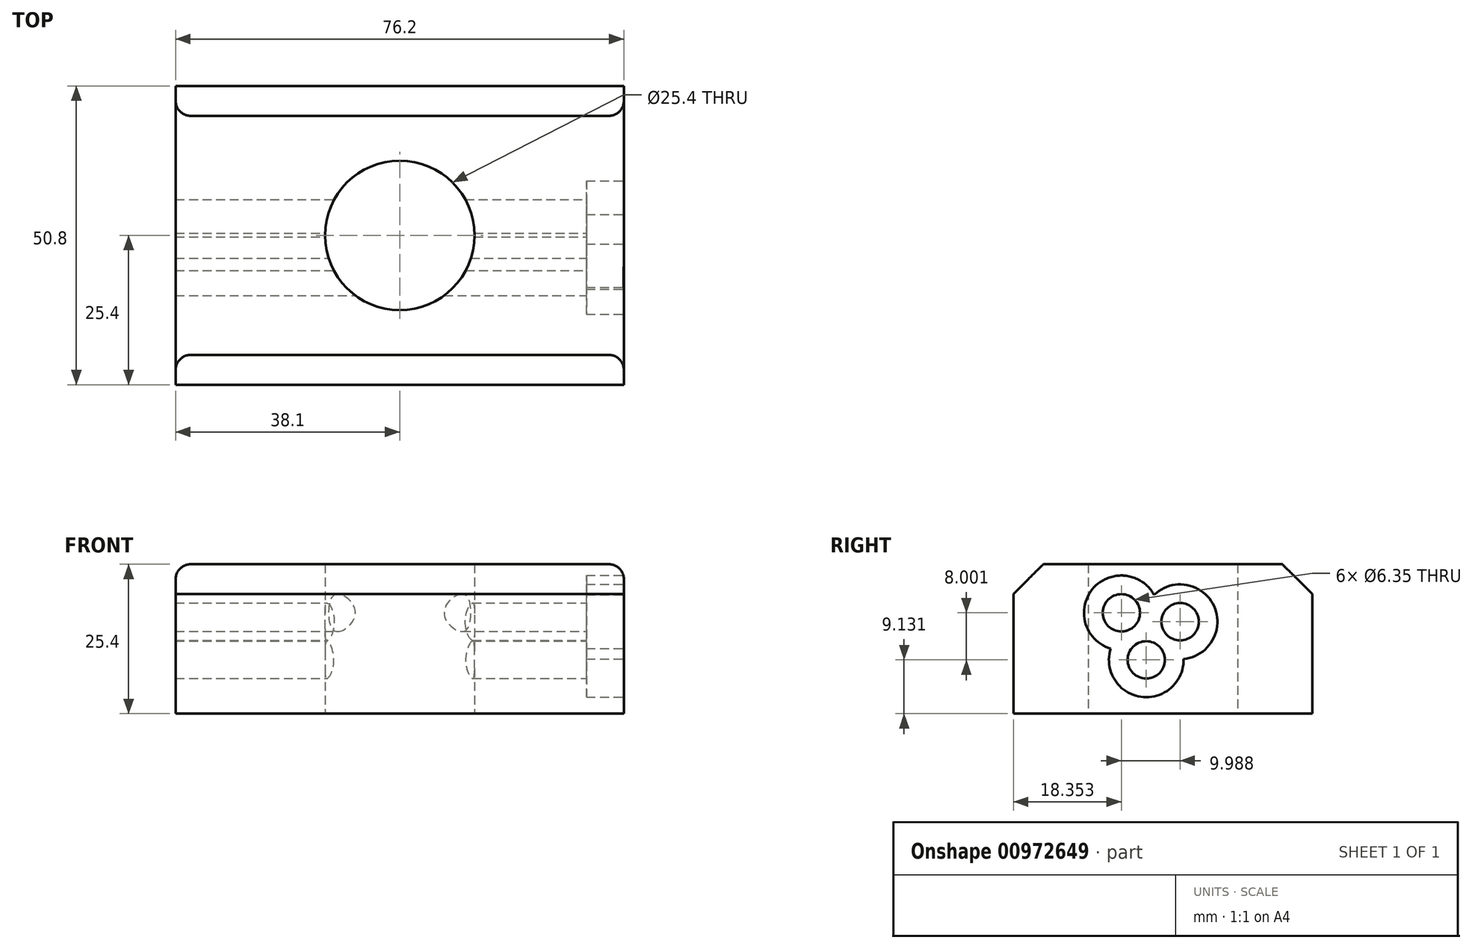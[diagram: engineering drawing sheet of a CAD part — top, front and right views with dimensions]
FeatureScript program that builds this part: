
annotation { "Feature Type Name" : "Feature", "Feature Type Description" : "" }
export const myFeature = defineFeature(function(context is Context, id is Id, definition is map)
    precondition{}
    {
        {
            var Q0;
            Q0=qCreatedBy(makeId("Top.planeOp"),FACE);
            var sketch = newSketch(context, id + "F0", { "sketchPlane" : qUnion([Q0])});
            skLineSegment(sketch, "E0.bottom", {"start": v(-38.1, 25.4) * mm, "end": v(38.1, 25.4) * mm});
            skLineSegment(sketch, "E0.top", {"start": v(-38.1, -25.4) * mm, "end": v(38.1, -25.4) * mm});
            skLineSegment(sketch, "E0.left", {"start": v(-38.1, 25.4) * mm, "end": v(-38.1, -25.4) * mm});
            skLineSegment(sketch, "E0.right", {"start": v(38.1, 25.4) * mm, "end": v(38.1, -25.4) * mm});
            skPoint(sketch, "E0.middle", {"position": v(0, 0) * mm});
            skCircle(sketch, "E1", {"center": v(0, 0) * mm, "radius": 12.7 * mm});
            skSolve(sketch);
        }
        {
            var Q0;
            Q0=makeQuery(id+"F0.imprint","IMPRINT",FACE,{"disambiguationData":[TD([[makeQuery(id+"F0.imprint","IMPRINT",EDGE,{"derivedFrom":sQuery(id+"F0.wireOp",EDGE,"E0.bottom")}),-1.0]])]});
            extrude(context, id + "F1", {"entities" : qUnion([Q0]), "depth" : 25.4 * mm, "offsetDistance" : 25.4 * mm});
        }
        {
            var Q0;
            Q0=makeQuery(id+"F1.opExtrude","SWEPT_FACE",FACE,{"disambiguationData":[OSD([sQuery(id+"F0.wireOp",EDGE,"E0.right")])]});
            var sketch = newSketch(context, id + "F2", { "sketchPlane" : qUnion([Q0])});
            skCircle(sketch, "E2", {"center": v(-2.34, 14.5) * mm, "radius": 5.4 * mm});
            skPoint(sketch, "E2.first.point", {"position": v(-7.05, 17.13) * mm});
            skPoint(sketch, "E2.second.point", {"position": v(2.94, 15.62) * mm});
            skPoint(sketch, "E2.third.point", {"position": v(-2.81, 9.13) * mm});
            skSolve(sketch);
        }
        {
            var Q0;
            Q0=sQuery(id+"F2.wireOp",VERTEX,"E2.first.point");
            var Q1;
            Q1=sQuery(id+"F2.wireOp",VERTEX,"E2.second.point");
            var Q2;
            Q2=sQuery(id+"F2.wireOp",VERTEX,"E2.third.point");
            var Q3;
            Q3=makeQuery(id+"F1.opExtrude","SWEPT_BODY",BODY,{"disambiguationData":[OSD([sQuery(id+"F0.wireOp",EDGE,"E0.bottom"),sQuery(id+"F0.wireOp",EDGE,"E0.top"),sQuery(id+"F0.wireOp",EDGE,"E0.left"),sQuery(id+"F0.wireOp",EDGE,"E0.right"),sQuery(id+"F0.wireOp",EDGE,"E1")])]});
            hole(context, id + "F3", {"style" : HoleStyle.C_BORE, "endStyle" : HoleEndStyle.THROUGH, "holeDiameter" : 6.35 * mm, "cBoreDiameter" : 12.7 * mm, "cBoreDepth" : 6.35 * mm, "majorDiameter" : 6.35 * mm, "isTappedThrough" : true, "tappedDepth" : 12.7 * mm, "tapClearance" : 3, "startFromSketch" : true, "locations" : qUnion([Q0, Q1, Q2]), "scope" : qUnion([Q3])});
        }
        {
            var Q0;
            Q0=makeQuery(id+"F1.opExtrude","CAP_EDGE",EDGE,{"disambiguationData":[OSD([sQuery(id+"F0.wireOp",EDGE,"E0.top")])],"isStart":false});
            var Q1;
            Q1=makeQuery(id+"F1.opExtrude","CAP_EDGE",EDGE,{"disambiguationData":[OSD([sQuery(id+"F0.wireOp",EDGE,"E0.bottom")])],"isStart":false});
            chamfer(context, id + "F4", {"entities" : qUnion([Q0, Q1]), "width" : 5.08 * mm, "tangentPropagation" : true});
        }
        {
            var Q0;
            Q0=makeQuery(id+"F1.opExtrude","CAP_EDGE",EDGE,{"disambiguationData":[OSD([sQuery(id+"F0.wireOp",EDGE,"E0.left")])],"isStart":false});
            fillet(context, id + "F5", {"entities" : qUnion([Q0]), "radius" : 2.54 * mm, "tangentPropagation" : true, "allowEdgeOverflow" : false});
        }
        {
            var Q0;
            Q0=makeQuery(id+"F1.opExtrude","CAP_EDGE",EDGE,{"disambiguationData":[OSD([sQuery(id+"F0.wireOp",EDGE,"E0.right")])],"isStart":false});
            var Q1;
            Q1=makeQuery(id+"F3.hole-1.boolean.opBoolean","COPY",EDGE,{"derivedFrom":makeQuery(id+"F3.hole-1.opRevolve","SWEPT_EDGE",EDGE,{"disambiguationData":[OSD([sQuery(id+"F3.hole-1.sketch.wireOp",EDGE,"cbore_start_line_2"),sQuery(id+"F3.hole-1.sketch.wireOp",EDGE,"cbore_start_line_3")])]})});
            var Q2;
            Q2=makeQuery(id+"F3.hole-0.boolean.opBoolean","COPY",EDGE,{"derivedFrom":makeQuery(id+"F3.hole-0.opRevolve","SWEPT_EDGE",EDGE,{"disambiguationData":[OSD([sQuery(id+"F3.hole-0.sketch.wireOp",EDGE,"cbore_start_line_2"),sQuery(id+"F3.hole-0.sketch.wireOp",EDGE,"cbore_start_line_3")])]})});
            var Q3;
            Q3=makeQuery(id+"F3.hole-2.boolean.opBoolean","COPY",EDGE,{"derivedFrom":makeQuery(id+"F3.hole-2.opRevolve","SWEPT_EDGE",EDGE,{"disambiguationData":[OSD([sQuery(id+"F3.hole-2.sketch.wireOp",EDGE,"cbore_start_line_2"),sQuery(id+"F3.hole-2.sketch.wireOp",EDGE,"cbore_start_line_3")])]})});
            fillet(context, id + "F6", {"entities" : qUnion([Q0, Q1, Q2, Q3]), "radius" : 2.54 * mm, "tangentPropagation" : true, "allowEdgeOverflow" : false});
        }
    });
